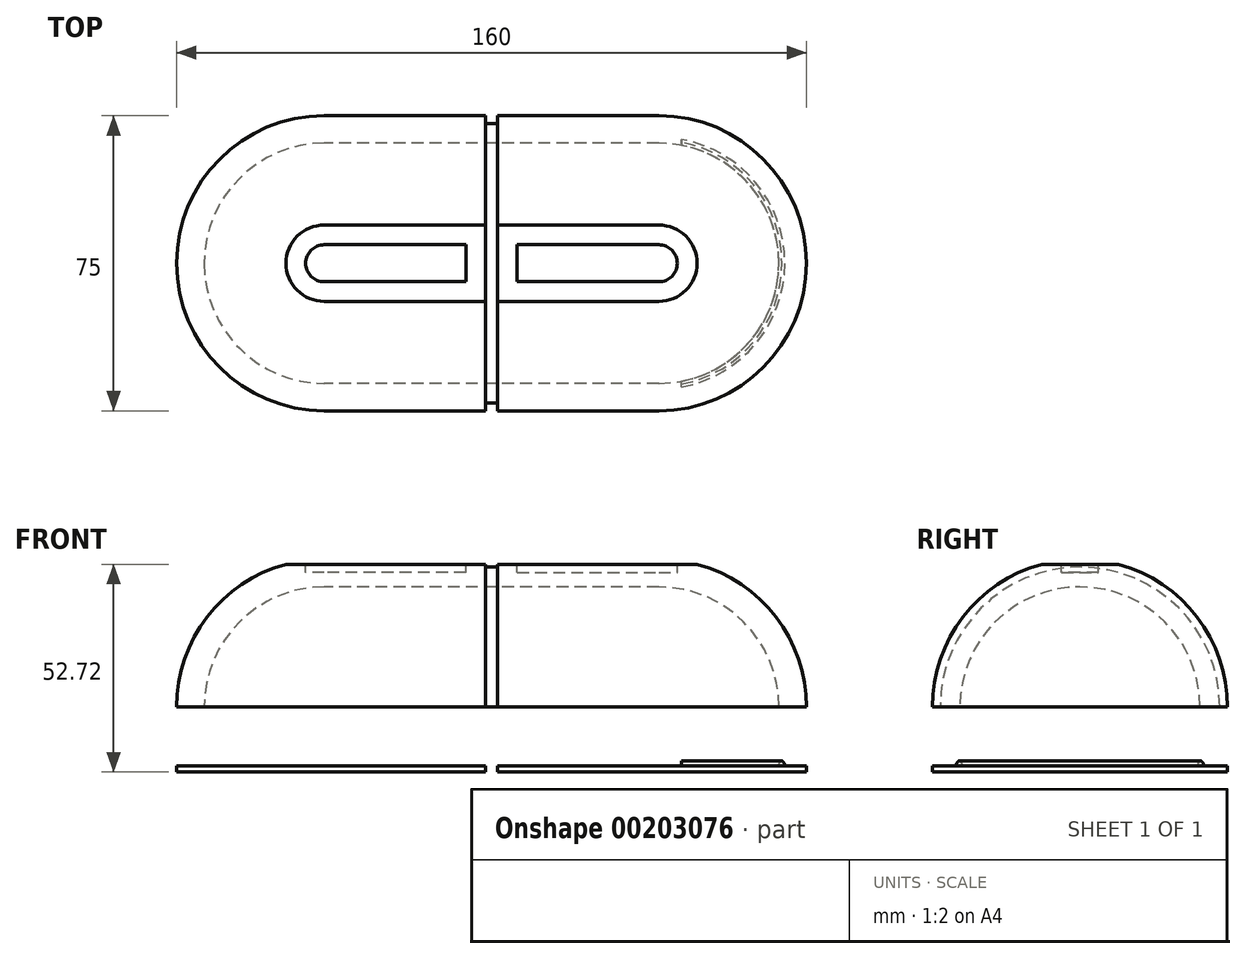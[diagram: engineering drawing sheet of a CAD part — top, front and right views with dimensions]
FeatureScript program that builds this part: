
annotation { "Feature Type Name" : "Feature", "Feature Type Description" : "" }
export const myFeature = defineFeature(function(context is Context, id is Id, definition is map)
    precondition{}
    {
        {
            var Q0;
            Q0=qCreatedBy(makeId("Top.planeOp"),FACE);
            var sketch = newSketch(context, id + "F0", { "sketchPlane" : qUnion([Q0])});
            skLineSegment(sketch, "E0.bottom", {"start": v(80, 37.5) * mm, "end": v(-80, 37.5) * mm});
            skLineSegment(sketch, "E0.top", {"start": v(42.5, -37.5) * mm, "end": v(1.5, -37.5) * mm});
            skLineSegment(sketch, "E0.left", {"start": v(80, 37.5) * mm, "end": v(80, -37.5) * mm});
            skLineSegment(sketch, "E0.right", {"start": v(-80, 37.5) * mm, "end": v(-80, 0) * mm});
            skPoint(sketch, "E0.middle", {"position": v(0, 0) * mm});
            skLineSegment(sketch, "E1", {"start": v(0, 0) * mm, "end": v(-73, 0) * mm, "construction": true});
            skLineSegment(sketch, "E2.MirrorCS", {"start": v(0, 0) * mm, "end": v(80, 0) * mm, "construction": true});
            skPoint(sketch, "E3", {"position": v(-42.5, -37.5) * mm});
            skArc(sketch, "E4", {"start": v(-80, 0) * mm, "mid": v(-69.02, -26.52) * mm, "end": v(-42.5, -37.5) * mm});
            skArc(sketch, "E5.MirrorCS", {"start": v(80, 0) * mm, "mid": v(69.02, -26.52) * mm, "end": v(42.5, -37.5) * mm});
            skLineSegment(sketch, "E6", {"start": v(0, -35.5) * mm, "end": v(-1.5, -35.5) * mm});
            skPoint(sketch, "E6.startSnap0", {"position": v(0, -37.5) * mm});
            skLineSegment(sketch, "E7", {"start": v(-1.5, -35.5) * mm, "end": v(-1.5, -37.5) * mm});
            skLineSegment(sketch, "E8.MirrorCS", {"start": v(0, -35.5) * mm, "end": v(1.5, -35.5) * mm});
            skLineSegment(sketch, "E9.MirrorCS", {"start": v(1.5, -35.5) * mm, "end": v(1.5, -37.5) * mm});
            skLineSegment(sketch, "E10.trimOffspring", {"start": v(-1.5, -37.5) * mm, "end": v(-42.5, -37.5) * mm});
            skPoint(sketch, "E11.orphan", {"position": v(-80, -37.5) * mm});
            skLineSegment(sketch, "E12.2", {"start": v(-75, 37.5) * mm, "end": v(-75, 22.3) * mm});
            skLineSegment(sketch, "E13.0", {"start": v(42.5, -30.5) * mm, "end": v(6.5, -30.5) * mm});
            skArc(sketch, "E13.1", {"start": v(73, 0) * mm, "mid": v(64.07, -21.57) * mm, "end": v(42.5, -30.5) * mm});
            skLineSegment(sketch, "E14", {"start": v(6.5, -30.5) * mm, "end": v(6.5, -30.5) * mm});
            skLineSegment(sketch, "E15.MirrorCS", {"start": v(-6.5, -30.5) * mm, "end": v(-6.5, -30.5) * mm});
            skLineSegment(sketch, "E16", {"start": v(80, 0) * mm, "end": v(73, 0) * mm});
            skArc(sketch, "E17.0", {"start": v(-73, 0) * mm, "mid": v(-64.07, -21.57) * mm, "end": v(-42.5, -30.5) * mm});
            skLineSegment(sketch, "E18", {"start": v(-80, 0) * mm, "end": v(-73, 0) * mm});
            skArc(sketch, "E19.MirrorCS", {"start": v(80, 0) * mm, "mid": v(69.02, 26.52) * mm, "end": v(42.5, 37.5) * mm});
            skLineSegment(sketch, "E20.MirrorCS", {"start": v(42.5, 37.5) * mm, "end": v(1.5, 37.5) * mm});
            skLineSegment(sketch, "E21.MirrorCS", {"start": v(-1.5, 37.5) * mm, "end": v(-42.5, 37.5) * mm});
            skArc(sketch, "E22.MirrorCS", {"start": v(-80, 0) * mm, "mid": v(-69.02, 26.52) * mm, "end": v(-42.5, 37.5) * mm});
            skLineSegment(sketch, "E23.MirrorCS", {"start": v(-1.5, 35.5) * mm, "end": v(-1.5, 37.5) * mm});
            skLineSegment(sketch, "E24.MirrorCS", {"start": v(1.5, 35.5) * mm, "end": v(1.5, 37.5) * mm});
            skLineSegment(sketch, "E25.MirrorCS", {"start": v(0, 35.5) * mm, "end": v(1.5, 35.5) * mm});
            skLineSegment(sketch, "E26.MirrorCS", {"start": v(0, 35.5) * mm, "end": v(-1.5, 35.5) * mm});
            skLineSegment(sketch, "E27", {"start": v(-1.5, -35.5) * mm, "end": v(-1.5, 35.5) * mm});
            skLineSegment(sketch, "E28", {"start": v(1.5, -35.5) * mm, "end": v(1.5, 35.5) * mm});
            skArc(sketch, "E29.MirrorCS", {"start": v(-73, 0) * mm, "mid": v(-64.07, 21.57) * mm, "end": v(-42.5, 30.5) * mm});
            skLineSegment(sketch, "E30.MirrorCS", {"start": v(-1.5, 30.5) * mm, "end": v(-42.5, 30.5) * mm});
            skLineSegment(sketch, "E31.MirrorCS", {"start": v(42.5, 30.5) * mm, "end": v(6.5, 30.5) * mm});
            skArc(sketch, "E32.MirrorCS", {"start": v(73, 0) * mm, "mid": v(64.07, 21.57) * mm, "end": v(42.5, 30.5) * mm});
            skLineSegment(sketch, "E33.MirrorCS", {"start": v(6.5, 30.5) * mm, "end": v(3, 30.5) * mm});
            skLineSegment(sketch, "E34.trimOffspring", {"start": v(-6.5, -30.5) * mm, "end": v(-42.5, -30.5) * mm});
            skPoint(sketch, "E17.1.start.orphan", {"position": v(-1.5, -30.5) * mm});
            skPoint(sketch, "E35.MirrorCS.end.orphan", {"position": v(-3, -30.5) * mm});
            skPoint(sketch, "E36.end.orphan", {"position": v(3, -30.5) * mm});
            skLineSegment(sketch, "E37", {"start": v(-6.5, -30.5) * mm, "end": v(6.5, -30.5) * mm});
            skLineSegment(sketch, "E38.MirrorCS", {"start": v(-6.5, 30.5) * mm, "end": v(6.5, 30.5) * mm});
            skSolve(sketch);
        }
        {
            var Q0;
            Q0=qCreatedBy(makeId("Right.planeOp"),FACE);
            var sketch = newSketch(context, id + "F1", { "sketchPlane" : qUnion([Q0])});
            skArc(sketch, "E39", {"start": v(37.5, 0) * mm, "mid": v(0, 37.5) * mm, "end": v(-37.5, 0) * mm});
            skPoint(sketch, "E40", {"position": v(-37.5, 0) * mm});
            skPoint(sketch, "E41", {"position": v(37.5, 0) * mm});
            skSolve(sketch);
        }
        {
            var Q0;
            Q0=makeQuery(id+"F0.imprint","IMPRINT",FACE,{"disambiguationData":[TD([[makeQuery(id+"F0.imprint","IMPRINT",EDGE,{"derivedFrom":sQuery(id+"F0.wireOp",EDGE,"E0.top")}),-1.0]])]});
            var Q1;
            Q1=makeQuery(id+"F0.imprint","IMPRINT",FACE,{"disambiguationData":[TD([[makeQuery(id+"F0.imprint","IMPRINT",EDGE,{"derivedFrom":sQuery(id+"F0.wireOp",EDGE,"E4")}),1.0]])]});
            var Q2;
            {var subQ5=sQuery(id+"F0.wireOp",EDGE,"E6");Q2=makeQuery(id+"F0.imprint","IMPRINT",FACE,{"disambiguationData":[TD([[makeQuery(id+"F0.imprint","IMPRINT",EDGE,{"derivedFrom":subQ5}),-1.0]])]});}
            var Q3;
            Q3=sQuery(id+"F1.wireOp",EDGE,"E39");
            sweep(context, id + "F2", {"profiles" : qUnion([Q0, Q1, Q2]), "path" : qUnion([Q3])});
        }
        {
            var Q0;
            Q0=makeQuery(id+"F0.imprint","IMPRINT",FACE,{"disambiguationData":[TD([[makeQuery(id+"F0.imprint","IMPRINT",EDGE,{"derivedFrom":sQuery(id+"F0.wireOp",EDGE,"E0.top")}),-1.0]])]});
            var Q1;
            {var subQ7=sQuery(id+"F0.wireOp",EDGE,"E13.0");Q1=makeQuery(id+"F0.imprint","IMPRINT",FACE,{"disambiguationData":[TD([[makeQuery(id+"F0.imprint","IMPRINT",EDGE,{"derivedFrom":subQ7}),-1.0]])]});}
            var Q2;
            Q2=makeQuery(id+"F0.imprint","IMPRINT",FACE,{"disambiguationData":[TD([[makeQuery(id+"F0.imprint","IMPRINT",EDGE,{"derivedFrom":sQuery(id+"F0.wireOp",EDGE,"E16")}),-1.0]])]});
            var Q3;
            Q3=makeQuery(id+"F0.imprint","IMPRINT",FACE,{"disambiguationData":[TD([[makeQuery(id+"F0.imprint","IMPRINT",EDGE,{"derivedFrom":sQuery(id+"F0.wireOp",EDGE,"E4")}),1.0]])]});
            var Q4;
            Q4=makeQuery(id+"F0.imprint","IMPRINT",FACE,{"disambiguationData":[TD([[makeQuery(id+"F0.imprint","IMPRINT",EDGE,{"derivedFrom":sQuery(id+"F0.wireOp",EDGE,"E17.0")}),1.0]])]});
            var Q5;
            Q5=makeQuery(id+"F0.imprint","IMPRINT",FACE,{"disambiguationData":[TD([[makeQuery(id+"F0.imprint","IMPRINT",EDGE,{"derivedFrom":sQuery(id+"F0.wireOp",EDGE,"E18")}),1.0]])]});
            extrude(context, id + "F3", {"entities" : qUnion([Q0, Q1, Q2, Q3, Q4, Q5]), "operationType" : NewBodyOperationType.ADD, "oppositeDirection" : true, "depth" : 16.5 * mm, "hasSecondDirection" : true, "secondDirectionOppositeDirection" : true, "secondDirectionDepth" : 15 * mm});
        }
        {
            var Q0;
            Q0=makeQuery(id+"F3.opExtrude","CAP_FACE",FACE,{"disambiguationData":[OSD([sQuery(id+"F0.wireOp",EDGE,"E0.top"),sQuery(id+"F0.wireOp",EDGE,"E5.MirrorCS"),sQuery(id+"F0.wireOp",EDGE,"E9.MirrorCS"),sQuery(id+"F0.wireOp",EDGE,"E19.MirrorCS"),sQuery(id+"F0.wireOp",EDGE,"E20.MirrorCS"),sQuery(id+"F0.wireOp",EDGE,"E24.MirrorCS"),sQuery(id+"F0.wireOp",EDGE,"E28")])],"isStart":true});
            var sketch = newSketch(context, id + "F4", { "sketchPlane" : qUnion([Q0])});
            skArc(sketch, "E42.0", {"start": v(48.28, -31.47) * mm, "mid": v(74.5, 0) * mm, "end": v(48.28, 31.47) * mm});
            skArc(sketch, "E43.0", {"start": v(48.28, -29.95) * mm, "mid": v(73, 0) * mm, "end": v(48.28, 29.95) * mm});
            skLineSegment(sketch, "E44", {"start": v(48.28, 31.47) * mm, "end": v(48.28, 29.95) * mm});
            skLineSegment(sketch, "E45", {"start": v(48.28, -31.47) * mm, "end": v(48.28, -29.95) * mm});
            skArc(sketch, "E46.MirrorCS", {"start": v(-48.28, -31.47) * mm, "mid": v(-74.5, 0) * mm, "end": v(-48.28, 31.47) * mm});
            skLineSegment(sketch, "E47.MirrorCS", {"start": v(-48.28, 31.47) * mm, "end": v(-48.28, 29.95) * mm});
            skArc(sketch, "E48.MirrorCS", {"start": v(-48.28, -29.95) * mm, "mid": v(-73, 0) * mm, "end": v(-48.28, 29.95) * mm});
            skLineSegment(sketch, "E49.MirrorCS", {"start": v(-48.28, -31.47) * mm, "end": v(-48.28, -29.95) * mm});
            skSolve(sketch);
        }
        {
            var Q0;
            Q0=makeQuery(id+"F4.imprint","IMPRINT",FACE,{"disambiguationData":[TD([[makeQuery(id+"F4.imprint","IMPRINT",EDGE,{"derivedFrom":sQuery(id+"F4.wireOp",EDGE,"E46.MirrorCS")}),-1.0]])]});
            var Q1;
            Q1=makeQuery(id+"F4.imprint","IMPRINT",FACE,{"disambiguationData":[TD([[makeQuery(id+"F4.imprint","IMPRINT",EDGE,{"derivedFrom":sQuery(id+"F4.wireOp",EDGE,"E42.0")}),1.0]])]});
            extrude(context, id + "F5", {"entities" : qUnion([Q0, Q1]), "operationType" : NewBodyOperationType.ADD, "depth" : 1.5 * mm});
        }
        {
            var Q0;
            Q0=makeQuery(id+"F5.opExtrude","CAP_EDGE",EDGE,{"disambiguationData":[OSD([sQuery(id+"F4.wireOp",EDGE,"E46.MirrorCS")])],"isStart":false});
            var Q1;
            Q1=makeQuery(id+"F5.opExtrude","CAP_EDGE",EDGE,{"disambiguationData":[OSD([sQuery(id+"F4.wireOp",EDGE,"E48.MirrorCS")])],"isStart":false});
            var Q2;
            Q2=makeQuery(id+"F5.opExtrude","CAP_EDGE",EDGE,{"disambiguationData":[OSD([sQuery(id+"F4.wireOp",EDGE,"E43.0")])],"isStart":false});
            var Q3;
            Q3=makeQuery(id+"F5.opExtrude","CAP_EDGE",EDGE,{"disambiguationData":[OSD([sQuery(id+"F4.wireOp",EDGE,"E42.0")])],"isStart":false});
            fillet(context, id + "F6", {"entities" : qUnion([Q0, Q1, Q2, Q3]), "radius" : 1.5 * mm, "tangentPropagation" : true, "allowEdgeOverflow" : false});
        }
        {
            var Q0;
            Q0=qCreatedBy(makeId("Right.planeOp"),FACE);
            var sketch = newSketch(context, id + "F7", { "sketchPlane" : qUnion([Q0])});
            skLineSegment(sketch, "E50.bottom", {"start": v(-12.6, 36.22) * mm, "end": v(12.6, 36.22) * mm});
            skLineSegment(sketch, "E50.top", {"start": v(-12.6, 40.22) * mm, "end": v(12.6, 40.22) * mm});
            skLineSegment(sketch, "E50.left", {"start": v(-12.6, 36.22) * mm, "end": v(-12.6, 40.22) * mm});
            skLineSegment(sketch, "E50.right", {"start": v(12.6, 36.22) * mm, "end": v(12.6, 40.22) * mm});
            skPoint(sketch, "E50.middle", {"position": v(0, 38.22) * mm});
            skSolve(sketch);
        }
        {
            var Q0;
            Q0 = qSketchRegion(id + "F7", true);
            extrude(context, id + "F8", {"entities" : qUnion([Q0]), "operationType" : NewBodyOperationType.REMOVE, "oppositeDirection" : true, "depth" : 80 * mm, "hasSecondDirection" : true, "secondDirectionOppositeDirection" : false, "secondDirectionDepth" : 80 * mm});
        }
        {
            var Q0;
            {var subQ0=sQuery(id+"F1.wireOp",EDGE,"E39");Q0=makeQuery(id+"F8.boolean.opBoolean","COPY",FACE,{"disambiguationData":[TD([makeQuery(id+"F2.opSweep","SWEPT_FACE",FACE,{"disambiguationData":[OSD([sQuery(id+"F0.wireOp",EDGE,"E0.top"),subQ0])]})])],"derivedFrom":makeQuery(id+"F8.opExtrude","SWEPT_FACE",FACE,{"disambiguationData":[OSD([sQuery(id+"F7.wireOp",EDGE,"E50.bottom")])]})});}
            var sketch = newSketch(context, id + "F9", { "sketchPlane" : qUnion([Q0])});
            skLineSegment(sketch, "E51.0", {"start": v(6.5, -4.7) * mm, "end": v(42.5, -4.7) * mm});
            skLineSegment(sketch, "E51.1", {"start": v(6.5, 4.7) * mm, "end": v(6.5, -4.7) * mm});
            skLineSegment(sketch, "E51.2", {"start": v(42.5, 4.7) * mm, "end": v(6.5, 4.7) * mm});
            skArc(sketch, "E51.3", {"start": v(42.5, -4.7) * mm, "mid": v(47.2, 0) * mm, "end": v(42.5, 4.7) * mm});
            skLineSegment(sketch, "E52.MirrorCS", {"start": v(-6.5, -4.7) * mm, "end": v(-42.5, -4.7) * mm});
            skLineSegment(sketch, "E53.MirrorCS", {"start": v(-6.5, 4.7) * mm, "end": v(-6.5, -4.7) * mm});
            skLineSegment(sketch, "E54.MirrorCS", {"start": v(-42.5, 4.7) * mm, "end": v(-6.5, 4.7) * mm});
            skArc(sketch, "E55.MirrorCS", {"start": v(-42.5, -4.7) * mm, "mid": v(-47.2, 0) * mm, "end": v(-42.5, 4.7) * mm});
            skSolve(sketch);
        }
        {
            var Q0;
            Q0=makeQuery(id+"F9.imprint","IMPRINT",FACE,{"disambiguationData":[TD([[makeQuery(id+"F9.imprint","IMPRINT",EDGE,{"derivedFrom":sQuery(id+"F9.wireOp",EDGE,"E51.0")}),1.0]])]});
            var Q1;
            Q1=makeQuery(id+"F9.imprint","IMPRINT",FACE,{"disambiguationData":[TD([[makeQuery(id+"F9.imprint","IMPRINT",EDGE,{"derivedFrom":sQuery(id+"F9.wireOp",EDGE,"E52.MirrorCS")}),-1.0]])]});
            extrude(context, id + "F10", {"entities" : qUnion([Q0, Q1]), "operationType" : NewBodyOperationType.REMOVE, "oppositeDirection" : true, "depth" : 2 * mm});
        }
    });
